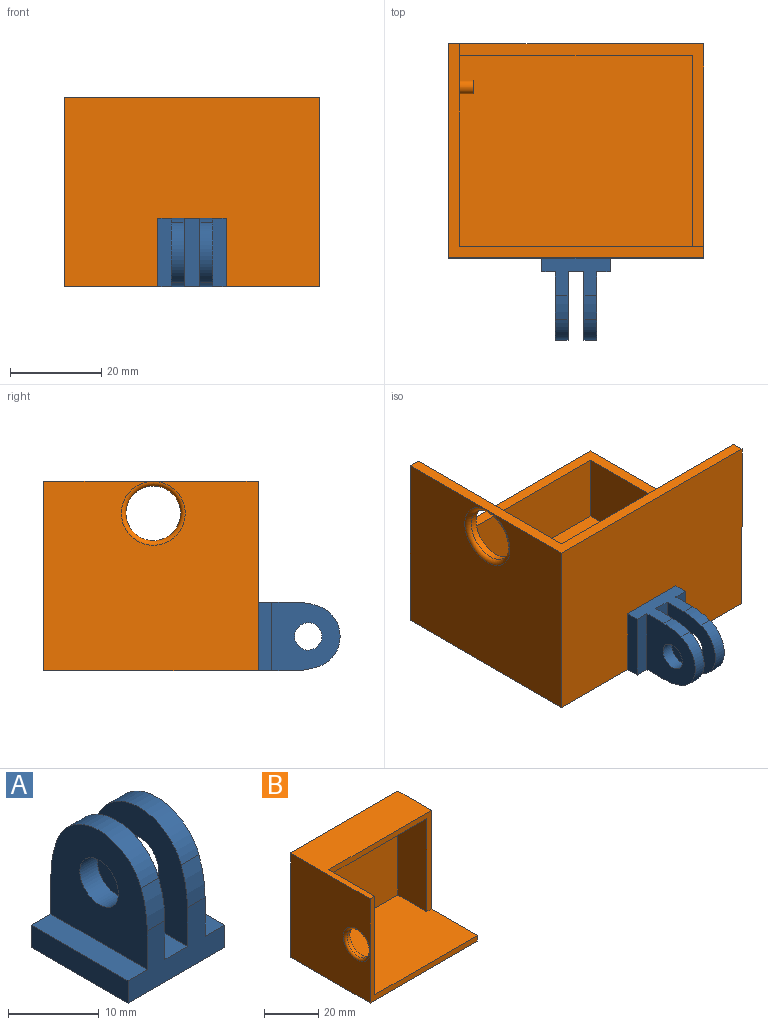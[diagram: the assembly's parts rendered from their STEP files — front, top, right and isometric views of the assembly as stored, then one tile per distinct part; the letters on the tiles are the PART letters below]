
ASSEMBLY  parts=2 mates=1
PART A: 20 faces, bbox 15x15x18 mm
  f0: plane 15x8.22mm, normal (0,1,0), area 73.7mm2, adj f2,f3,f4,f5,f6,f7,f8,f9
  f1: plane 15x8.22mm, normal (0,-1,0), area 73.7mm2, adj f2,f3,f4,f5,f6,f7,f8,f9
  f2: plane 15x3mm, normal (0,0,1), area 45mm2, adj f0,f1,f4,f10
  f3: plane 15x3.5mm, normal (0,0,1), area 52.5mm2, adj f0,f1,f8,f11
  f4: plane 15x3mm, normal (1,0,0), area 45mm2, adj f0,f1,f2,f7
  f5: plane 15x3mm, normal (-1,0,0), area 45mm2, adj f0,f1,f6,f7
  f6: plane 15x3mm, normal (0,0,1), area 45mm2, adj f0,f1,f5,f9
  f7: plane 15x15mm, normal (0,0,-1), area 225mm2, adj f0,f1,f4,f5
  f8: plane 15x15mm, normal (1,0,0), area 168.6mm2, adj f0,f1,f3,f12,f14,f18,f19
  f9: plane 15x15mm, normal (-1,0,0), area 168.6mm2, adj f0,f1,f6,f12,f14,f18,f19
  f10: plane 15x15mm, normal (1,0,0), area 168.6mm2, adj f0,f1,f2,f13,f15,f16,f17
  f11: plane 15x15mm, normal (-1,0,0), area 168.6mm2, adj f0,f1,f3,f13,f15,f16,f17
  f12: cylinder r=3mm len=6mm, axis (1,0,0), area 51.8mm2, adj f8,f9
  f13: cylinder r=3mm len=6mm, axis (-1,0,0), area 51.8mm2, adj f10,f11
  f14: cylinder r=7mm len=13.07mm, axis (1,0,0), area 46.3mm2, adj f8,f9,f18,f19
  f15: cylinder r=7mm len=13.07mm, axis (-1,0,0), area 46.3mm2, adj f10,f11,f16,f17
  f16: cylinder r=15mm len=5.3mm, axis (-1,0,0), area 14.9mm2, adj f0,f10,f11,f15
  f17: cylinder r=15mm len=5.3mm, axis (-1,0,0), area 14.9mm2, adj f1,f10,f11,f15
  f18: cylinder r=15mm len=5.3mm, axis (1,0,0), area 14.9mm2, adj f0,f8,f9,f14
  f19: cylinder r=15mm len=5.3mm, axis (1,0,0), area 14.9mm2, adj f1,f8,f9,f14
PART B: 16 faces, bbox 56x42.1x47 mm
  f0: plane 53.5x44.5mm, normal (0,-1,0), area 238.7mm2, adj f3,f8,f10,f11,f12,f13
  f1: plane 56x47mm, normal (0,-1,0), area 251.3mm2, adj f2,f3,f7,f8,f10,f13
  f2: plane 56x41.5mm, normal (0,0,-1), area 2324mm2, adj f1,f4,f7,f13
  f3: plane 53.5x39mm, normal (0,0,1), area 2049mm2, adj f0,f1,f5,f8,f12,f13
  f4: plane 56x47mm, normal (0,1,0), area 2632mm2, adj f2,f7,f10,f13
  f5: plane 51x42mm, normal (0,-1,0), area 2142mm2, adj f3,f8,f11,f12
  f6: cylinder r=6mm len=12mm, axis (1,0,0), area 56.5mm2, adj f8,f9
  f7: plane 47x41.5mm, normal (-1,0,0), area 1796.6mm2, adj f1,f2,f4,f9,f10
  f8: plane 44.5x39mm, normal (1,0,0), area 1577.8mm2, adj f0,f1,f3,f5,f6,f10,f11,f14
  f9: torus R=7mm, axis (-1,0,0), area 62.8mm2, adj f6,f7
  f10: plane 56x41.5mm, normal (0,0,1), area 1040mm2, adj f0,f1,f4,f7,f8,f13
  f11: plane 51x15mm, normal (0,0,-1), area 765mm2, adj f0,f5,f8,f12
  f12: plane 42x15mm, normal (-1,0,0), area 630mm2, adj f0,f3,f5,f11
  f13: plane 47x41.5mm, normal (1,0,0), area 882.5mm2, adj f0,f1,f2,f3,f4,f10
  f14: cylinder r=1.5mm len=3mm, axis (-1,0,0), area 28.3mm2, adj f8,f15
  f15: plane 3x3mm, normal (1,0,0), area 7.1mm2, adj f14
PLACE A rot(axis=(1,0,0),90deg) t=(-5.42,-32.15,-10.43)mm
PLACE B rot(axis=(-1,0,0),90deg) t=(-5.42,-29.65,4.07)mm
MATE planar B.f2 <-> A.f7  axis (0,-1,0) through (-5.42,-32.15,-17.93)mm
